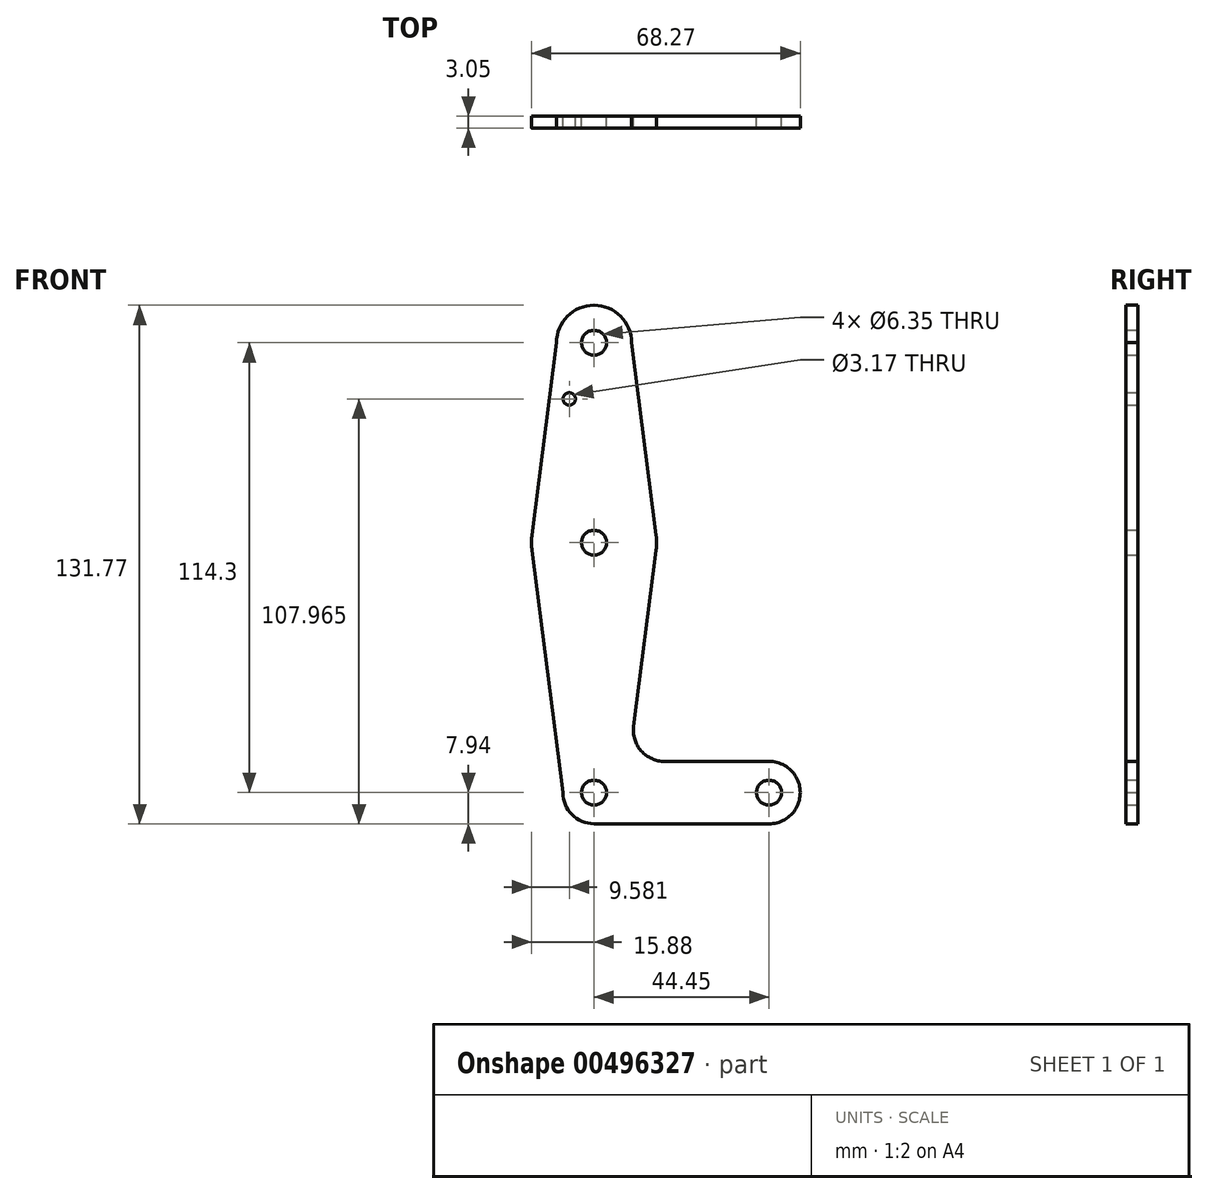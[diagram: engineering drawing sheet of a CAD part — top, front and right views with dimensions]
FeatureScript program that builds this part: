
annotation { "Feature Type Name" : "Feature", "Feature Type Description" : "" }
export const myFeature = defineFeature(function(context is Context, id is Id, definition is map)
    precondition{}
    {
        {
            var Q0;
            Q0=qCreatedBy(makeId("Front.planeOp"),FACE);
            var sketch = newSketch(context, id + "F0", { "sketchPlane" : qUnion([Q0])});
            skLineSegment(sketch, "E0", {"start": v(0, 0) * mm, "end": v(0, 114.3) * mm, "construction": true});
            skLineSegment(sketch, "E1", {"start": v(0, 0) * mm, "end": v(44.45, 0) * mm, "construction": true});
            skCircle(sketch, "E2", {"center": v(44.45, 0) * mm, "radius": 7.94 * mm});
            skCircle(sketch, "E3", {"center": v(0, 0) * mm, "radius": 7.9 * mm});
            skCircle(sketch, "E4", {"center": v(0, 114.3) * mm, "radius": 9.53 * mm});
            skCircle(sketch, "E5", {"center": v(0, 63.5) * mm, "radius": 15.88 * mm});
            skLineSegment(sketch, "E6", {"start": v(9.52, 114.3) * mm, "end": v(15.75, 65.5) * mm});
            skLineSegment(sketch, "E7", {"start": v(-9.53, 114.3) * mm, "end": v(-15.75, 65.5) * mm});
            skLineSegment(sketch, "E8", {"start": v(15.75, 61.5) * mm, "end": v(10.06, 16.87) * mm});
            skLineSegment(sketch, "E9", {"start": v(-7.9, 0) * mm, "end": v(-15.75, 61.5) * mm});
            skLineSegment(sketch, "E10", {"start": v(44.44, 7.94) * mm, "end": v(17.95, 7.92) * mm});
            skLineSegment(sketch, "E11", {"start": v(0, -7.9) * mm, "end": v(44.44, -7.94) * mm});
            skCircle(sketch, "E12", {"center": v(0, 114.3) * mm, "radius": 3.18 * mm});
            skCircle(sketch, "E13", {"center": v(0, 63.5) * mm, "radius": 3.18 * mm});
            skCircle(sketch, "E14", {"center": v(0, 0) * mm, "radius": 3.18 * mm});
            skCircle(sketch, "E15", {"center": v(44.45, 0) * mm, "radius": 3.18 * mm});
            skCircle(sketch, "E16", {"center": v(-6.3, 100.03) * mm, "radius": 1.59 * mm});
            skArc(sketch, "E17.filletArc", {"start": v(10.06, 16.87) * mm, "mid": v(11.98, 10.61) * mm, "end": v(17.95, 7.92) * mm});
            skSolve(sketch);
        }
        {
            var Q0;
            Q0 = qSketchRegion(id + "F0", true);
            extrude(context, id + "F1", {"entities" : qUnion([Q0]), "depth" : 3.05 * mm});
        }
    });
